# Revit family: Haworth_BeHold_Modular_AttachedStorageForHAT
name_source: partatom
category: Furniture Systems
revit_build: Autodesk Revit 2018 (Build: 20170223_1515(x64)
units: mm (PartAtom-declared; Revit-internal decimal feet)

## family parameters
Always vertical = Yes
Cut with Voids When Loaded = No
OmniClass Number = 23.40.70.14.64.21
OmniClass Title = Systems Furniture
Part Type = Normal
Room Calculation Point = No
Round Connector Dimension = Use Diameter
Shared = No
Work Plane-Based = No

## types (4) — shared parameters
Actual Height = 22"
Assembly Code = E2020200
Bottom Case Offset = 1/2"
Case Thickness = 3/4"
Custom Size = No
Description = Haworth - Be_Hold - Attached Storage For HAT
Glide Finish = Haworth _ Polymer _ Slate
Manufacturer = Haworth
Max. Depth = 24"
Max. Height = 22"
Max. Width = 36"
Min. Depth = 16"
Min. Height = 22"
Min. Width = 30"
Model = Haworth Be_Hold
Revision Number = 1
Separator Back Offset = 9 3/16"
Shelf 1 Offset = 13 5/16"
Shelf Finish = Haworth _ Paint _ Sky Blue
Size = Verify Final Dim. w/ Haworth
Standard Depths = 16, 24 in.
Standard Widths = 30, 36 in.
Sustainability Info = https://www.haworth.com
Top Case Front Control = 3"
Top Thickness = 3/4"
Trim Finish = Haworth _ Paint _ Sky Blue
URL = www.haworth.com
URL - Product = http://www.haworth.com
Void Back Offset = 3 15/16"
Void Dimension = 4"
Warranty = http://www.haworth.com

## per-type parameters (varying)
| type | Actual Bag Liner | Actual Cutout | Actual Depth | Actual Steel Shelf | Actual Width | Back Case Back Control | Back Case Side Control | Bag Liner | Cutout | Cutout Dimension | Depth | Inset Style | Proud Style | Shelf | Shelf Control | Side Case Back Control | Top Case Back Control | Width |
| Inset Back - 24d 36w | No | Yes | 24" | No | 36" | 3/16" | 3/4" | No | Yes | 11 3/16" | 24" | Yes | No | No | Yes | 0" | 3/16" | 36" |
| Inset Back - 24d 30w | No | Yes | 24" | No | 30" | 3/16" | 3/4" | No | Yes | 11 3/16" | 24" | Yes | No | No | Yes | 0" | 3/16" | 30" |
| Proud Back - 16d 36w | Yes | No | 16" | Yes | 36" | 0" | 0" | Yes | No | 1/2" | 16" | No | Yes | Yes | No | 3/4" | 0" | 36" |
| Proud Back - 16d 30w | Yes | No | 16" | Yes | 30" | 0" | 0" | Yes | No | 1/2" | 16" | No | Yes | Yes | No | 3/4" | 0" | 30" |

## geometry (parser evidence)
native form markers: Sweep x5
no freeform markers — native parametric forms only
